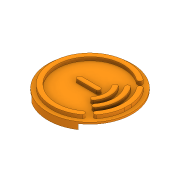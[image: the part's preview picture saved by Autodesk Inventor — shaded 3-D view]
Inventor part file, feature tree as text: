
AUTODESK INVENTOR PART (.ipt)
format: ipt  version: 2020.3 (Build 243373000, 373)  size: 193,536 bytes
history: native  units: mm
features: extrude x4, sketch x4
ambient origin geometry x8: Origin, YZ Plane, XZ Plane, XY Plane, X Axis, Y Axis, Z Axis, Center Point
bodies: Solid1 (feature_tree)
feature tree (8):
  extrude  "Extrusion1"  Depth=2.0mm
  extrude  "Extrusion2"  Depth=1.0mm TaperAngle=0.0deg
  sketch  "Sketch3"  dims[d7=60.0mm d8=40.0mm]
  extrude  "Extrusion3"  Depth=40.0mm
  extrude  "Extrusion4"  Depth=10.0mm
  sketch  "Sketch1"  dims[d0=48.0mm d2=2.0mm]
  sketch  "Sketch2"  dims[d3=4.0mm d4=0.0mm d5=1.0mm d6=0.0mm]
  sketch  "Sketch4"  dims[d10=40.0mm d11=48.0mm d12=44.0mm d13=34.0mm d14=28.0mm d15=22.0mm d16=14.0mm d17=8.0mm d18=38.074mm d19=2.65912mm d20=2.65912mm d21=2.65912mm d22=2.417382mm d23=2.417382mm d24=1.369mm d25=2.659266mm d26=1.352mm d27=1.351mm d28=2.0mm d29=0.0mm d30=10.0mm d31=0.0mm]
